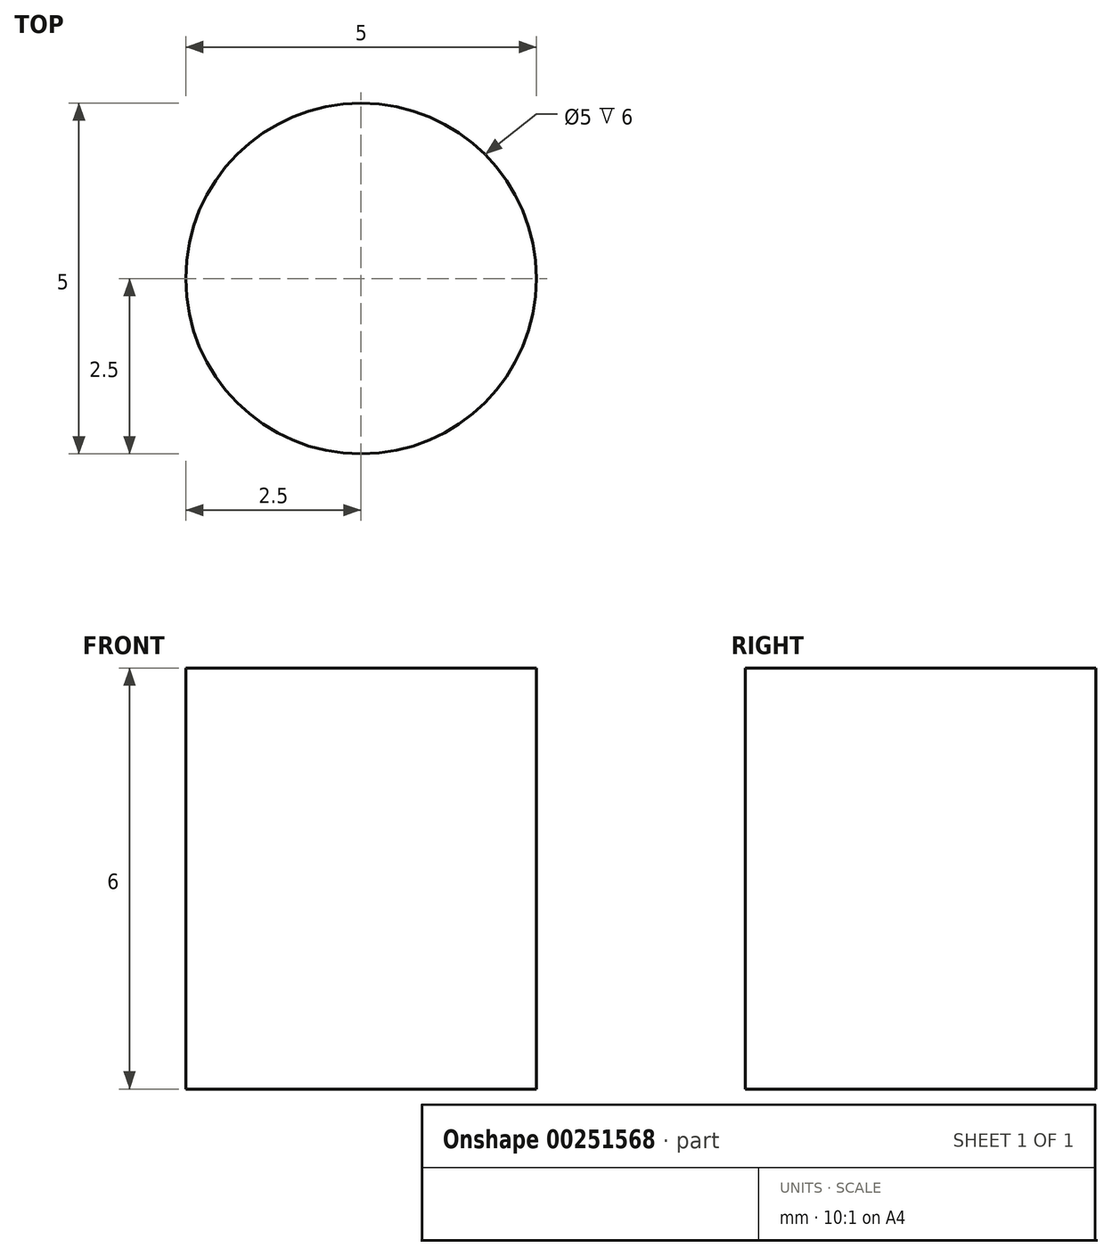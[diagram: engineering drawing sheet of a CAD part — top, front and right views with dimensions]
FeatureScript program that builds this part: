
annotation { "Feature Type Name" : "Feature", "Feature Type Description" : "" }
export const myFeature = defineFeature(function(context is Context, id is Id, definition is map)
    precondition{}
    {
        {
            var Q0;
            Q0=qCreatedBy(makeId("Front.planeOp"),FACE);
            var sketch = newSketch(context, id + "F0", { "sketchPlane" : qUnion([Q0])});
            skLineSegment(sketch, "E0", {"start": v(0, 9.32) * mm, "end": v(2.5, 9.32) * mm});
            skLineSegment(sketch, "E1", {"start": v(2.5, 9.32) * mm, "end": v(2.5, 3.32) * mm});
            skLineSegment(sketch, "E2", {"start": v(2.5, 3.32) * mm, "end": v(0, 3.32) * mm});
            skLineSegment(sketch, "E3", {"start": v(0, 17.7) * mm, "end": v(0, -4.42) * mm});
            skSolve(sketch);
        }
        {
            var Q0;
            Q0=sQuery(id+"F0.wireOp",EDGE,"E0");
            var Q1;
            Q1=sQuery(id+"F0.wireOp",EDGE,"E1");
            var Q2;
            Q2=sQuery(id+"F0.wireOp",EDGE,"E2");
            var Q3;
            Q3=sQuery(id+"F0.wireOp",EDGE,"E3");
            revolve(context, id + "F1", {"bodyType" : ToolBodyType.SURFACE, "surfaceEntities" : qUnion([Q0, Q1, Q2]), "axis" : qUnion([Q3]), "revolveType" : RevolveType.FULL});
        }
    });
